# Revit family: Doors_Garage_Asta-America_600-Series
name_source: partatom
category: Doors
units: mm (PartAtom-declared; Revit-internal decimal feet)

## family parameters
Always vertical = Yes
Cut with Voids When Loaded = No
Host = Wall
OmniClass Number = 23.30.10.17.27.11
OmniClass Title = Overhead Coiling
Room Calculation Point = No
Shared = No

## types (7) — shared parameters
2 = Guide Type : 2
2(W/L) = Guide Type : 2(W/L)
3 = Guide Type : 3
3(W/L) = Guide Type : 3(W/L)
4 = Guide Type : 4
4(W/L) = Guide Type : 4(W/L)
5(W/L) = Guide Type : 5(W/L)
6(W/L) = Guide Type : 6(W/L)
Assembly Code = B2030400
Bottom Bar = Asta America - Steel
Curtain Slats = Asta America - Steel - Powder Coat - Grey Topcoat
Description = ASTA AMERICA 600 Series Insulated Service Doors
Edition number = 1
Function = Exterior
Gauge = Gauge : 18
Guide Height = 16' - 9 25/128"
Guides = Asta America - Steel
Height = 15' - 0"
Height Control = 15' - 0"
Hood = Asta America - Steel - Galvanized
Keynote = 08110
Manufacturer = Asta America
Model = 600 Series Insulated Service Doors
Motor Visibility Left = No
Motor Visibility Right = Yes
No of Curtain Slats = 86
Opening Height = 15' - 0"
Operator Height = 15' - 4 49/64"
Part Slat Number = 64
Product Guid = df891233-9bdb-46c9-bfc9-37c0687376c0
Product data url = https://www.bimobject.com
Sizing Disclaimer = The 600 Series is available in sizes 40’ x 16’ to 28’ x 26’ (varies by model).
Slat Height = 0' - 2 21/256"
Slat Offset = 3' - 9 103/128"
URL = www.astaamerica.com
Wall Closure = By host
Windload = Available design to +/- 50 PSF for 16’ wide (22-gauge). Windload varies by size and model; for windload
availability on large sizes contact customer service.

## per-type parameters (varying)
| type | Between Jambs | Face of Wall | Opening Width | Operator | Rough Height | Slat Distance | Width | wPanels |
| Between Jamb with Chain Hoist | Yes | No | 12' - 0" | Operator : Chain Hoist (BJ) | 16' - 9 25/128" | 0' - 5 229/256" | 12' - 0" | No |
| Between Jamb with GH Motor | Yes | No | 12' - 0" | Operator : GH Motor | 16' - 9 25/128" | 0' - 5 229/256" | 12' - 0" | No |
| Face of Wall with Chain Hoist | No | Yes | 12' - 0" | Operator : Chain Hoist (FW) | 15' - 0" | 0' - 0" | 12' - 0" | No |
| Face of Wall with Chain Hoist and Vision Lites | No | Yes | 11' - 0" | Operator : Chain Hoist (FW) | 15' - 0" | 0' - 0" | 11' - 0" | Yes |
| Face of Wall with H Motor | No | Yes | 12' - 0" | Operator : H Motor | 15' - 0" | 0' - 0" | 12' - 0" | No |
| Face of Wall with GH Motor | No | Yes | 12' - 0" | Operator : GH Motor | 15' - 0" | 0' - 0" | 12' - 0" | No |
| Face of Wall with GH Motor and Vision Lites | No | Yes | 12' - 0" | Operator : GH Motor | 15' - 0" | 0' - 0" | 12' - 0" | Yes |

## geometry (parser evidence)
native form markers: Blend x2, Sweep x18
no freeform markers — native parametric forms only
